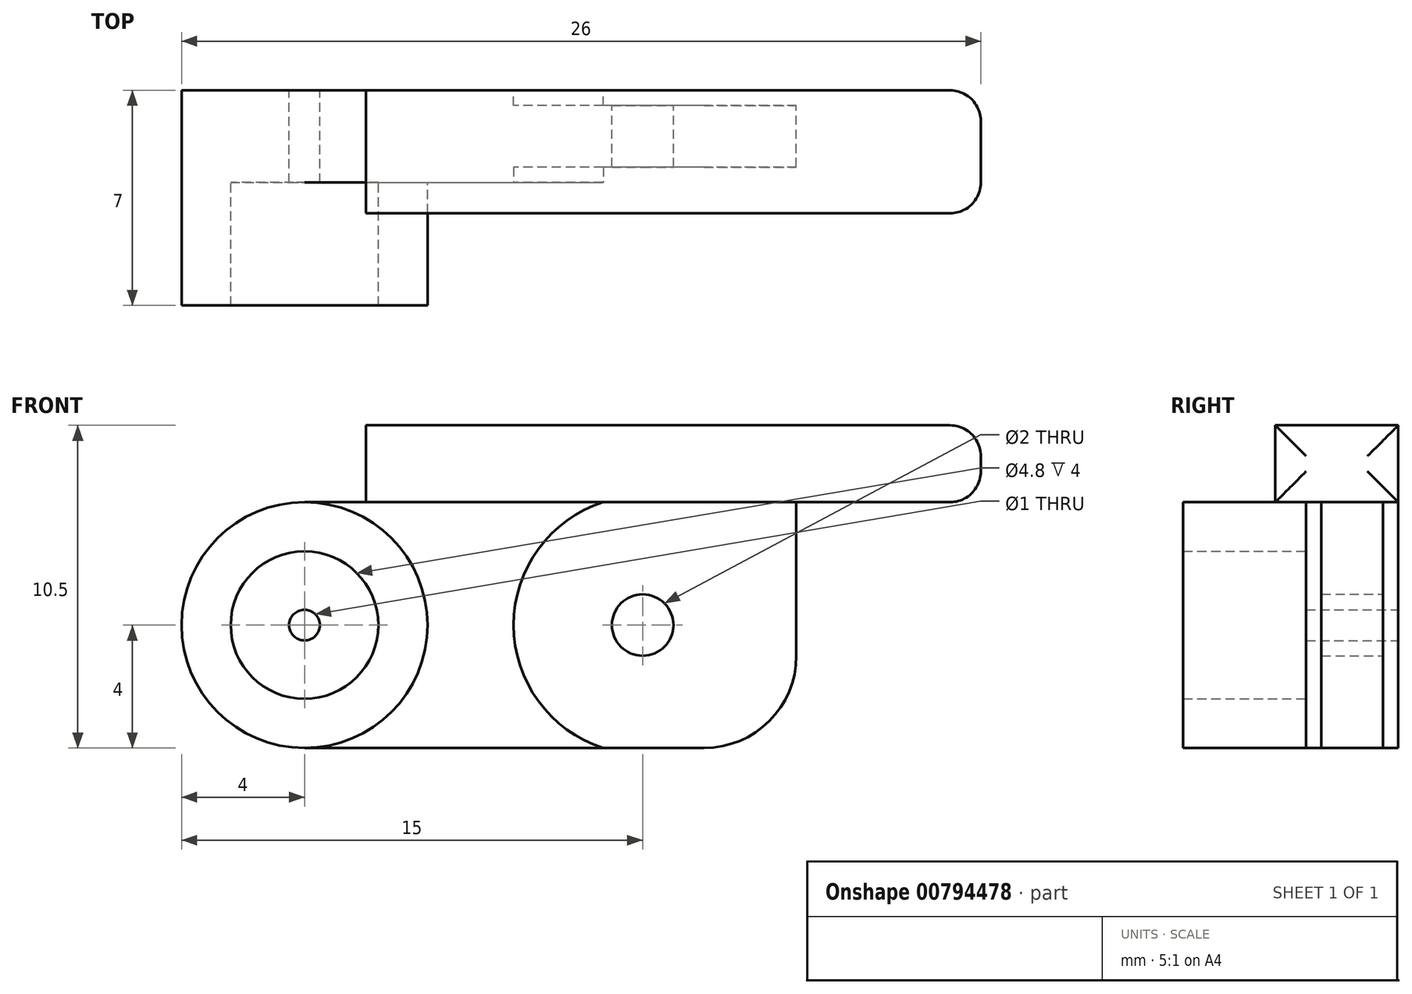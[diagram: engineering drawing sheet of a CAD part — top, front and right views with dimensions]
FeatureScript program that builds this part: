
annotation { "Feature Type Name" : "Feature", "Feature Type Description" : "" }
export const myFeature = defineFeature(function(context is Context, id is Id, definition is map)
    precondition{}
    {
        {
            var Q0;
            Q0=qCreatedBy(makeId("Front.planeOp"),FACE);
            var sketch = newSketch(context, id + "F0", { "sketchPlane" : qUnion([Q0])});
            skCircle(sketch, "E0", {"center": v(0, 0) * mm, "radius": 2.4 * mm});
            skCircle(sketch, "E1", {"center": v(0, 0) * mm, "radius": 4 * mm});
            skCircle(sketch, "E2", {"center": v(0, 0) * mm, "radius": 0.5 * mm});
            skPoint(sketch, "E3.start.orphan", {"position": v(0, 2.4) * mm});
            skLineSegment(sketch, "E4", {"start": v(0, 0) * mm, "end": v(16, 0) * mm, "construction": true});
            skLineSegment(sketch, "E5", {"start": v(16, 0) * mm, "end": v(16, 4) * mm});
            skLineSegment(sketch, "E6", {"start": v(0, 4) * mm, "end": v(16, 4) * mm});
            skLineSegment(sketch, "E7.MirrorCS", {"start": v(0, -4) * mm, "end": v(16, -4) * mm});
            skPoint(sketch, "E8.orphan", {"position": v(26, 8.15) * mm});
            skPoint(sketch, "E9.orphan", {"position": v(16, 0) * mm});
            skPoint(sketch, "E10.MirrorCS.end.orphan", {"position": v(16, -4) * mm});
            skLineSegment(sketch, "E11.MirrorCS", {"start": v(16, 0) * mm, "end": v(16, -4) * mm});
            skPoint(sketch, "E12.MirrorCS.end.orphan", {"position": v(26, -8.15) * mm});
            skCircle(sketch, "E13", {"center": v(11, 0) * mm, "radius": 1 * mm});
            skLineSegment(sketch, "E14.bottom", {"start": v(6, 4) * mm, "end": v(22, 4) * mm});
            skLineSegment(sketch, "E14.top", {"start": v(2, 6.5) * mm, "end": v(22, 6.5) * mm});
            skLineSegment(sketch, "E14.left", {"start": v(2, 4) * mm, "end": v(2, 6.5) * mm});
            skLineSegment(sketch, "E14.right", {"start": v(22, 4) * mm, "end": v(22, 6.5) * mm});
            skSolve(sketch);
        }
        {
            var Q0;
            {var subQ4=sQuery(id+"F0.wireOp",EDGE,"E5");Q0=makeQuery(id+"F0.imprint","IMPRINT",FACE,{"disambiguationData":[TD([[makeQuery(id+"F0.imprint","IMPRINT",EDGE,{"derivedFrom":subQ4}),1.0]])]});}
            extrude(context, id + "F1", {"entities" : qUnion([Q0]), "depth" : 3 * mm, "offsetDistance" : 25 * mm});
        }
        {
            var Q0;
            Q0=makeQuery(id+"F0.imprint","IMPRINT",FACE,{"disambiguationData":[TD([[makeQuery(id+"F0.imprint","IMPRINT",EDGE,{"derivedFrom":sQuery(id+"F0.wireOp",EDGE,"E0")}),-1.0]])]});
            extrude(context, id + "F2", {"entities" : qUnion([Q0]), "operationType" : NewBodyOperationType.ADD, "depth" : 7 * mm, "offsetDistance" : 25 * mm});
        }
        {
            var Q0;
            Q0=makeQuery(id+"F0.imprint","IMPRINT",FACE,{"disambiguationData":[TD([[makeQuery(id+"F0.imprint","IMPRINT",EDGE,{"derivedFrom":sQuery(id+"F0.wireOp",EDGE,"E0")}),1.0]])]});
            extrude(context, id + "F3", {"entities" : qUnion([Q0]), "operationType" : NewBodyOperationType.ADD, "depth" : 3 * mm, "offsetDistance" : 25 * mm});
        }
        {
            var Q0;
            Q0=qCreatedBy(makeId("Front.planeOp"),FACE);
            cPlane(context, id + "F4", {"entities" : qUnion([Q0]), "cplaneType" : CPlaneType.OFFSET, "offset" : 3 * mm, "width" : 150 * mm, "height" : 150 * mm});
        }
        {
            var Q0;
            Q0=qCreatedBy(makeId("Front.planeOp"),FACE);
            var sketch = newSketch(context, id + "F5", { "sketchPlane" : qUnion([Q0])});
            skLineSegment(sketch, "E15.bottom", {"start": v(19.39, 4) * mm, "end": v(9.72, 4) * mm});
            skLineSegment(sketch, "E15.top", {"start": v(19.39, -4) * mm, "end": v(9.72, -4) * mm});
            skLineSegment(sketch, "E15.left", {"start": v(19.39, 4) * mm, "end": v(19.39, -4) * mm});
            skPoint(sketch, "E15.middle", {"position": v(14.55, 0) * mm});
            skArc(sketch, "E16", {"start": v(9.72, 4) * mm, "mid": v(6.8, 0) * mm, "end": v(9.72, -4) * mm});
            skSolve(sketch);
        }
        {
            var Q0;
            Q0=makeQuery(id+"F5.imprint","IMPRINT",FACE,{"disambiguationData":[TD([[makeQuery(id+"F5.imprint","IMPRINT",EDGE,{"derivedFrom":sQuery(id+"F5.wireOp",EDGE,"E15.bottom")}),1.0]])]});
            extrude(context, id + "F6", {"entities" : qUnion([Q0]), "operationType" : NewBodyOperationType.REMOVE, "depth" : 0.5 * mm, "offsetDistance" : 25 * mm});
        }
        {
            var Q0;
            Q0=makeQuery(id+"F0.imprint","IMPRINT",FACE,{"disambiguationData":[TD([[makeQuery(id+"F0.imprint","IMPRINT",EDGE,{"derivedFrom":sQuery(id+"F0.wireOp",EDGE,"E14.top")}),-1.0]])]});
            extrude(context, id + "F7", {"entities" : qUnion([Q0]), "operationType" : NewBodyOperationType.ADD, "depth" : 4 * mm, "offsetDistance" : 25 * mm});
        }
        {
            var Q0;
            Q0=makeQuery(id+"F1.opExtrude","SWEPT_EDGE",EDGE,{"disambiguationData":[OSD([sQuery(id+"F0.wireOp",EDGE,"E7.MirrorCS"),sQuery(id+"F0.wireOp",EDGE,"E11.MirrorCS")])]});
            fillet(context, id + "F8", {"entities" : qUnion([Q0]), "radius" : 3 * mm, "tangentPropagation" : true, "allowEdgeOverflow" : false});
        }
        {
            var Q0;
            Q0=makeQuery(id+"F7.opExtrude","SWEPT_EDGE",EDGE,{"disambiguationData":[OSD([sQuery(id+"F0.wireOp",EDGE,"E14.bottom"),sQuery(id+"F0.wireOp",EDGE,"E14.right")])]});
            var Q1;
            Q1=makeQuery(id+"F7.opExtrude","CAP_EDGE",EDGE,{"disambiguationData":[OSD([sQuery(id+"F0.wireOp",EDGE,"E14.right")])],"isStart":false});
            var Q2;
            Q2=makeQuery(id+"F7.opExtrude","CAP_EDGE",EDGE,{"disambiguationData":[OSD([sQuery(id+"F0.wireOp",EDGE,"E14.right")])],"isStart":true});
            var Q3;
            Q3=makeQuery(id+"F7.opExtrude","SWEPT_EDGE",EDGE,{"disambiguationData":[OSD([sQuery(id+"F0.wireOp",EDGE,"E14.top"),sQuery(id+"F0.wireOp",EDGE,"E14.right")])]});
            fillet(context, id + "F9", {"entities" : qUnion([Q0, Q1, Q2, Q3]), "radius" : 1 * mm, "tangentPropagation" : true, "allowEdgeOverflow" : false});
        }
        {
            var Q0;
            Q0=qCreatedBy(id+"F4.planeOp",FACE);
            var sketch = newSketch(context, id + "F10", { "sketchPlane" : qUnion([Q0])});
            skLineSegment(sketch, "E17.bottom", {"start": v(19.39, 4) * mm, "end": v(9.72, 4) * mm});
            skLineSegment(sketch, "E17.top", {"start": v(19.39, -4) * mm, "end": v(9.72, -4) * mm});
            skLineSegment(sketch, "E17.left", {"start": v(19.39, 4) * mm, "end": v(19.39, -4) * mm});
            skPoint(sketch, "E17.middle", {"position": v(14.55, 0) * mm});
            skArc(sketch, "E18", {"start": v(9.72, 4) * mm, "mid": v(6.8, 0) * mm, "end": v(9.72, -4) * mm});
            skSolve(sketch);
        }
        {
            var Q0;
            Q0=makeQuery(id+"F10.imprint","IMPRINT",FACE,{"disambiguationData":[TD([[makeQuery(id+"F10.imprint","IMPRINT",EDGE,{"derivedFrom":sQuery(id+"F10.wireOp",EDGE,"E17.bottom")}),1.0]])]});
            extrude(context, id + "F11", {"entities" : qUnion([Q0]), "operationType" : NewBodyOperationType.REMOVE, "oppositeDirection" : true, "depth" : 0.5 * mm, "offsetDistance" : 25 * mm});
        }
    });
